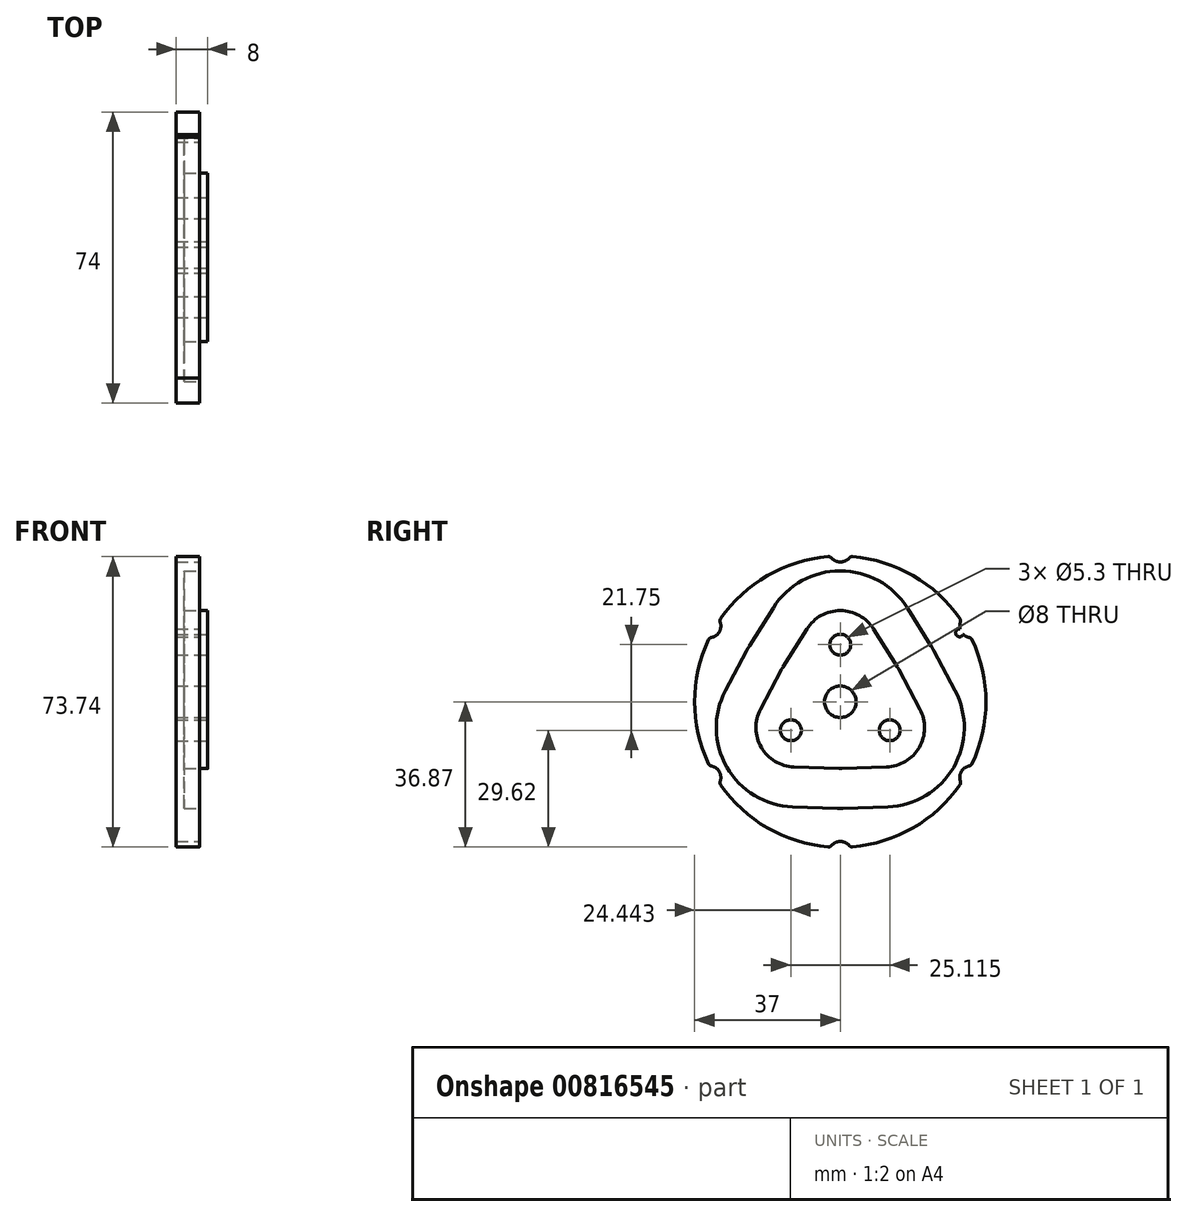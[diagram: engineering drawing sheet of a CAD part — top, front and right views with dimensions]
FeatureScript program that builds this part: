
annotation { "Feature Type Name" : "Feature", "Feature Type Description" : "" }
export const myFeature = defineFeature(function(context is Context, id is Id, definition is map)
    precondition{}
    {
        {
            var Q0;
            Q0=qCreatedBy(makeId("Right.planeOp"),FACE);
            var sketch = newSketch(context, id + "F0", { "sketchPlane" : qUnion([Q0])});
            skArc(sketch, "E0", {"start": v(-3.09, 36.87) * mm, "mid": v(-18.5, 32.04) * mm, "end": v(-30.39, 21.1) * mm});
            skCircle(sketch, "E1", {"center": v(0, 0) * mm, "radius": 4 * mm});
            skLineSegment(sketch, "E2", {"start": v(0, 50.53) * mm, "end": v(0, -45.3) * mm, "construction": true});
            skLineSegment(sketch, "E3", {"start": v(0, 0) * mm, "end": v(28.08, 48.64) * mm, "construction": true});
            skLineSegment(sketch, "E4", {"start": v(0, 0) * mm, "end": v(48.73, -28.13) * mm, "construction": true});
            skLineSegment(sketch, "E5.MirrorCS", {"start": v(0, 0) * mm, "end": v(-28.08, 48.64) * mm, "construction": true});
            skLineSegment(sketch, "E6.MirrorCS", {"start": v(-43.76, 25.27) * mm, "end": v(32.04, -18.5) * mm, "construction": true});
            skLineSegment(sketch, "E7.MirrorCS", {"start": v(0, 0) * mm, "end": v(-28.08, -48.64) * mm, "construction": true});
            skLineSegment(sketch, "E8.MirrorCS", {"start": v(0, 0) * mm, "end": v(28.08, -48.64) * mm, "construction": true});
            skLineSegment(sketch, "E9", {"start": v(-8.48, 18.48) * mm, "end": v(-14.54, 8.81) * mm});
            skLineSegment(sketch, "E10", {"start": v(-14.9, 8.18) * mm, "end": v(-20.25, -1.9) * mm});
            skLineSegment(sketch, "E11", {"start": v(-11.78, -16.58) * mm, "end": v(-0.36, -17) * mm});
            skLineSegment(sketch, "E12", {"start": v(0.36, -17) * mm, "end": v(11.77, -16.58) * mm});
            skLineSegment(sketch, "E13", {"start": v(20.24, -1.9) * mm, "end": v(14.9, 8.18) * mm});
            skLineSegment(sketch, "E14", {"start": v(14.53, 8.8) * mm, "end": v(8.47, 18.48) * mm});
            skPoint(sketch, "E15.visualSharp", {"position": v(0, 32) * mm});
            skArc(sketch, "E15.filletArc", {"start": v(8.47, 18.48) * mm, "mid": v(0, 23.17) * mm, "end": v(-8.48, 18.48) * mm});
            skPoint(sketch, "E16.visualSharp", {"position": v(-14.73, 8.5) * mm});
            skArc(sketch, "E16.filletArc", {"start": v(-14.54, 8.81) * mm, "mid": v(-14.73, 8.5) * mm, "end": v(-14.9, 8.18) * mm});
            skPoint(sketch, "E17.visualSharp", {"position": v(-27.71, -16) * mm});
            skArc(sketch, "E17.filletArc", {"start": v(-20.25, -1.9) * mm, "mid": v(-20.07, -11.59) * mm, "end": v(-11.78, -16.58) * mm});
            skPoint(sketch, "E18.visualSharp", {"position": v(0, -17.01) * mm});
            skArc(sketch, "E18.filletArc", {"start": v(-0.36, -17) * mm, "mid": v(0, -17) * mm, "end": v(0.36, -17) * mm});
            skPoint(sketch, "E19.visualSharp", {"position": v(27.71, -16) * mm});
            skArc(sketch, "E19.filletArc", {"start": v(11.77, -16.58) * mm, "mid": v(20.07, -11.59) * mm, "end": v(20.24, -1.9) * mm});
            skPoint(sketch, "E20.visualSharp", {"position": v(14.72, 8.5) * mm});
            skArc(sketch, "E20.filletArc", {"start": v(14.9, 8.18) * mm, "mid": v(14.72, 8.5) * mm, "end": v(14.53, 8.8) * mm});
            skLineSegment(sketch, "E21.0", {"start": v(-17.03, 23.85) * mm, "end": v(-23.1, 14.18) * mm});
            skArc(sketch, "E21.1", {"start": v(-0.73, -27.1) * mm, "mid": v(0, -27.1) * mm, "end": v(0.73, -27.1) * mm});
            skLineSegment(sketch, "E21.2", {"start": v(-12.14, -26.67) * mm, "end": v(-0.73, -27.1) * mm});
            skArc(sketch, "E21.3", {"start": v(-29.17, 2.82) * mm, "mid": v(-28.82, -16.64) * mm, "end": v(-12.14, -26.67) * mm});
            skLineSegment(sketch, "E21.4", {"start": v(-23.83, 12.91) * mm, "end": v(-29.17, 2.82) * mm});
            skLineSegment(sketch, "E21.5", {"start": v(0.73, -27.1) * mm, "end": v(12.14, -26.68) * mm});
            skArc(sketch, "E21.6", {"start": v(-23.1, 14.18) * mm, "mid": v(-23.47, 13.55) * mm, "end": v(-23.83, 12.91) * mm});
            skArc(sketch, "E21.7", {"start": v(12.14, -26.68) * mm, "mid": v(28.81, -16.63) * mm, "end": v(29.16, 2.83) * mm});
            skLineSegment(sketch, "E21.8", {"start": v(29.16, 2.83) * mm, "end": v(23.81, 12.91) * mm});
            skArc(sketch, "E21.9", {"start": v(23.81, 12.91) * mm, "mid": v(23.46, 13.55) * mm, "end": v(23.09, 14.17) * mm});
            skLineSegment(sketch, "E21.10", {"start": v(23.09, 14.17) * mm, "end": v(17.03, 23.84) * mm});
            skArc(sketch, "E21.11", {"start": v(17.03, 23.84) * mm, "mid": v(0, 33.27) * mm, "end": v(-17.03, 23.85) * mm});
            skCircle(sketch, "E22", {"center": v(0, 0) * mm, "radius": 14.5 * mm, "construction": true});
            skCircle(sketch, "E23", {"center": v(-12.56, -7.25) * mm, "radius": 2.65 * mm});
            skCircle(sketch, "E24", {"center": v(12.56, -7.25) * mm, "radius": 2.65 * mm});
            skCircle(sketch, "E25", {"center": v(0, 14.5) * mm, "radius": 2.65 * mm});
            skArc(sketch, "E26", {"start": v(30.45, 18.5) * mm, "mid": v(29.44, 17) * mm, "end": v(31.24, 17.13) * mm});
            skArc(sketch, "E27", {"start": v(-2.25, 36.53) * mm, "mid": v(0, 35.5) * mm, "end": v(2.25, 36.53) * mm});
            skPoint(sketch, "E28.visualSharp", {"position": v(-2.53, 36.91) * mm});
            skArc(sketch, "E28.filletArc", {"start": v(-2.25, 36.53) * mm, "mid": v(-2.63, 36.8) * mm, "end": v(-3.09, 36.87) * mm});
            skPoint(sketch, "E29.visualSharp", {"position": v(2.53, 36.91) * mm});
            skArc(sketch, "E29.filletArc", {"start": v(3.09, 36.87) * mm, "mid": v(2.63, 36.8) * mm, "end": v(2.25, 36.53) * mm});
            skPoint(sketch, "E30.center.orphan", {"position": v(0, -35) * mm});
            skArc(sketch, "E31.MirrorCS", {"start": v(32.76, 16.32) * mm, "mid": v(33.19, 16.12) * mm, "end": v(33.48, 15.76) * mm});
            skArc(sketch, "E32.MirrorCS", {"start": v(30.39, 21.1) * mm, "mid": v(30.56, 20.68) * mm, "end": v(30.51, 20.22) * mm});
            skPoint(sketch, "E33.MirrorP", {"position": v(33.23, 16.26) * mm});
            skArc(sketch, "E34.MirrorCS", {"start": v(32.76, 16.32) * mm, "mid": v(31.94, 16.6) * mm, "end": v(31.24, 17.13) * mm});
            skPoint(sketch, "E35.MirrorP", {"position": v(30.7, 20.65) * mm});
            skArc(sketch, "E36.trimOffspring", {"start": v(30.39, 21.1) * mm, "mid": v(18.5, 32.04) * mm, "end": v(3.09, 36.87) * mm});
            skLineSegment(sketch, "E37.trimOffspring", {"start": v(31.18, 18) * mm, "end": v(-39.22, -22.65) * mm, "construction": true});
            skArc(sketch, "E38.trimOffspring", {"start": v(30.45, 18.5) * mm, "mid": v(30.35, 19.36) * mm, "end": v(30.51, 20.22) * mm});
            skArc(sketch, "E39.MirrorCS", {"start": v(-30.51, 20.22) * mm, "mid": v(-30.56, 20.68) * mm, "end": v(-30.39, 21.1) * mm});
            skArc(sketch, "E40.MirrorCS", {"start": v(-33.48, 15.76) * mm, "mid": v(-33.19, 16.12) * mm, "end": v(-32.76, 16.32) * mm});
            skPoint(sketch, "E41.MirrorP", {"position": v(-33.23, 16.26) * mm});
            skPoint(sketch, "E42.MirrorP", {"position": v(-30.7, 20.65) * mm});
            skArc(sketch, "E43.MirrorCS", {"start": v(-30.51, 20.22) * mm, "mid": v(-30.75, 17.75) * mm, "end": v(-32.76, 16.32) * mm});
            skArc(sketch, "E44.trimOffspring", {"start": v(-33.48, 15.76) * mm, "mid": v(-37, 0) * mm, "end": v(-33.48, -15.76) * mm});
            skArc(sketch, "E45.MirrorCS", {"start": v(-33.48, -15.76) * mm, "mid": v(-33.19, -16.12) * mm, "end": v(-32.76, -16.32) * mm});
            skArc(sketch, "E46.MirrorCS", {"start": v(-30.51, -20.22) * mm, "mid": v(-30.56, -20.68) * mm, "end": v(-30.39, -21.1) * mm});
            skPoint(sketch, "E47.MirrorP", {"position": v(-30.7, -20.65) * mm});
            skArc(sketch, "E48.MirrorCS", {"start": v(-30.51, -20.22) * mm, "mid": v(-30.75, -17.75) * mm, "end": v(-32.76, -16.32) * mm});
            skPoint(sketch, "E49.MirrorP", {"position": v(-33.23, -16.26) * mm});
            skArc(sketch, "E50.trimOffspring", {"start": v(-30.39, -21.1) * mm, "mid": v(-18.5, -32.04) * mm, "end": v(-3.09, -36.87) * mm});
            skArc(sketch, "E51.MirrorCS", {"start": v(3.09, -36.87) * mm, "mid": v(2.63, -36.8) * mm, "end": v(2.25, -36.53) * mm});
            skArc(sketch, "E52.MirrorCS", {"start": v(-2.25, -36.53) * mm, "mid": v(-2.63, -36.8) * mm, "end": v(-3.09, -36.87) * mm});
            skArc(sketch, "E53.MirrorCS", {"start": v(-2.25, -36.53) * mm, "mid": v(0, -35.5) * mm, "end": v(2.25, -36.53) * mm});
            skPoint(sketch, "E54.MirrorP", {"position": v(-2.53, -36.91) * mm});
            skPoint(sketch, "E55.MirrorP", {"position": v(2.53, -36.91) * mm});
            skArc(sketch, "E56.trimOffspring", {"start": v(3.09, -36.87) * mm, "mid": v(18.5, -32.04) * mm, "end": v(30.39, -21.1) * mm});
            skPoint(sketch, "E57.orphan", {"position": v(39.22, -22.65) * mm});
            skPoint(sketch, "E58.MirrorCS.start.orphan", {"position": v(43.76, 25.27) * mm});
            skArc(sketch, "E59.MirrorCS", {"start": v(30.39, -21.1) * mm, "mid": v(30.56, -20.68) * mm, "end": v(30.51, -20.22) * mm});
            skArc(sketch, "E60.MirrorCS", {"start": v(32.76, -16.32) * mm, "mid": v(33.19, -16.12) * mm, "end": v(33.48, -15.76) * mm});
            skPoint(sketch, "E61.MirrorP", {"position": v(33.23, -16.26) * mm});
            skPoint(sketch, "E62.MirrorP", {"position": v(30.7, -20.65) * mm});
            skPoint(sketch, "E63.MirrorP", {"position": v(30.31, -17.5) * mm});
            skArc(sketch, "E64.MirrorCS", {"start": v(32.76, -16.32) * mm, "mid": v(30.75, -17.75) * mm, "end": v(30.51, -20.22) * mm});
            skArc(sketch, "E65.trimOffspring", {"start": v(33.48, -15.76) * mm, "mid": v(37, 0) * mm, "end": v(33.48, 15.76) * mm});
            skSolve(sketch);
        }
        {
            var Q0;
            Q0=qSketchRegion(id+"F0",true);
            var Q1;
            Q1=makeQuery(id+"F0.imprint","IMPRINT",FACE,{"disambiguationData":[TD([[makeQuery(id+"F0.imprint","IMPRINT",EDGE,{"derivedFrom":sQuery(id+"F0.wireOp",EDGE,"E9")}),-1.0]])]});
            var Q2;
            Q2=makeQuery(id+"F0.imprint","IMPRINT",FACE,{"disambiguationData":[TD([[makeQuery(id+"F0.imprint","IMPRINT",EDGE,{"derivedFrom":sQuery(id+"F0.wireOp",EDGE,"E1")}),-1.0]])]});
            extrude(context, id + "F1", {"entities" : qUnion([Q0, Q1, Q2]), "oppositeDirection" : true, "depth" : 6 * mm, "offsetDistance" : 25 * mm});
        }
        {
            var Q0;
            Q0=makeQuery(id+"F0.imprint","IMPRINT",FACE,{"disambiguationData":[TD([[makeQuery(id+"F0.imprint","IMPRINT",EDGE,{"derivedFrom":sQuery(id+"F0.wireOp",EDGE,"E9")}),-1.0]])]});
            extrude(context, id + "F2", {"entities" : qUnion([Q0]), "operationType" : NewBodyOperationType.REMOVE, "oppositeDirection" : true, "depth" : 4 * mm, "offsetDistance" : 25 * mm});
        }
        {
            var Q0;
            {var subQ0=sQuery(id+"F0.wireOp",EDGE,"E1");Q0=makeQuery(id+"F2.boolean.opBoolean","SPLIT",FACE,{"disambiguationData":[TD([makeQuery(id+"F1.opExtrude","SWEPT_FACE",FACE,{"disambiguationData":[OSD([subQ0])]})])],"derivedFrom":makeQuery(id+"F1.opExtrude","CAP_FACE",FACE,{"disambiguationData":[OSD([sQuery(id+"F0.wireOp",EDGE,"E0"),subQ0])],"isStart":true})});}
            extrude(context, id + "F3", {"entities" : qUnion([Q0]), "operationType" : NewBodyOperationType.ADD, "depth" : 2 * mm, "offsetDistance" : 25 * mm});
        }
    });
